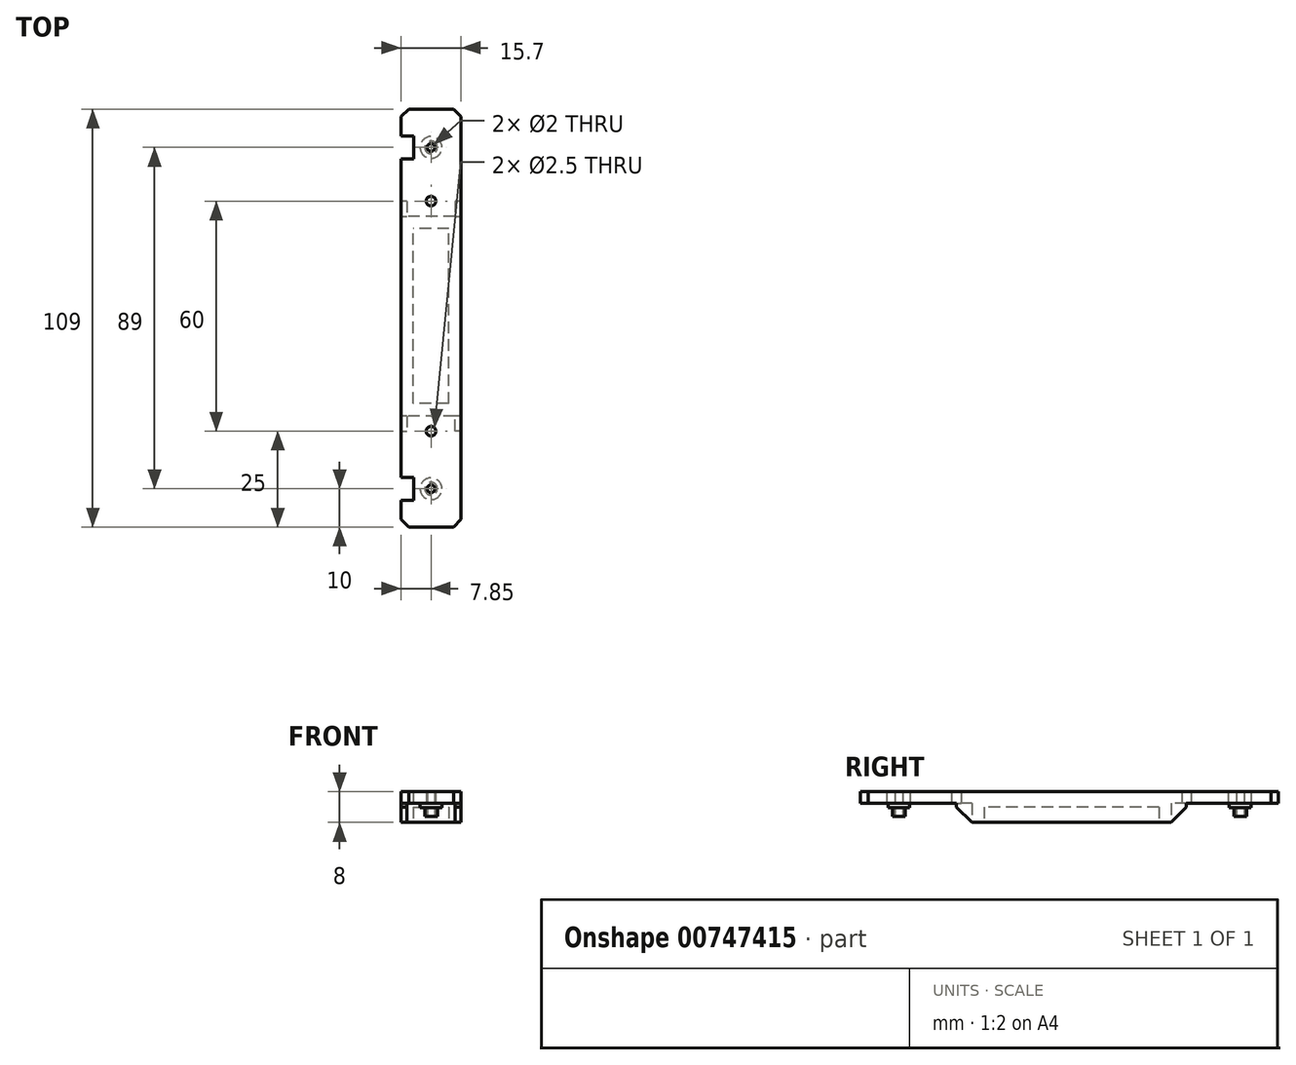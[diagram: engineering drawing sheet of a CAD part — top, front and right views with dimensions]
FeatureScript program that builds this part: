
annotation { "Feature Type Name" : "Feature", "Feature Type Description" : "" }
export const myFeature = defineFeature(function(context is Context, id is Id, definition is map)
    precondition{}
    {
        {
            var Q0;
            Q0=qCreatedBy(makeId("Right.planeOp"),FACE);
            var sketch = newSketch(context, id + "F0", { "sketchPlane" : qUnion([Q0])});
            skLineSegment(sketch, "E0", {"start": v(-25, 5) * mm, "end": v(0, 5) * mm});
            skLineSegment(sketch, "E1", {"start": v(0, 5) * mm, "end": v(0, 0) * mm});
            skLineSegment(sketch, "E2", {"start": v(60, 0) * mm, "end": v(60, 5) * mm});
            skLineSegment(sketch, "E3", {"start": v(60, 5) * mm, "end": v(84, 5) * mm});
            skLineSegment(sketch, "E4", {"start": v(84, 5) * mm, "end": v(84, 8) * mm});
            skLineSegment(sketch, "E5", {"start": v(-25, 8) * mm, "end": v(-25, 5) * mm});
            skLineSegment(sketch, "E6.trimOffspring", {"start": v(84, 8) * mm, "end": v(-25, 8) * mm});
            skLineSegment(sketch, "E7", {"start": v(0, 0) * mm, "end": v(0, 0) * mm});
            skLineSegment(sketch, "E8", {"start": v(0, 0) * mm, "end": v(60, 0) * mm});
            skSolve(sketch);
        }
        {
            var Q0;
            Q0=qSketchRegion(id+"F0",true);
            extrude(context, id + "F1", {"entities" : qUnion([Q0]), "depth" : 15.7 * mm, "offsetDistance" : 25 * mm, "symmetric" : true});
        }
        {
            var Q0;
            Q0=makeQuery(id+"F1.opExtrude","CAP_EDGE",EDGE,{"disambiguationData":[OSD([sQuery(id+"F0.wireOp",EDGE,"E5")])],"isStart":false});
            var Q1;
            Q1=makeQuery(id+"F1.opExtrude","CAP_EDGE",EDGE,{"disambiguationData":[OSD([sQuery(id+"F0.wireOp",EDGE,"E5")])],"isStart":true});
            var Q2;
            Q2=makeQuery(id+"F1.opExtrude","CAP_EDGE",EDGE,{"disambiguationData":[OSD([sQuery(id+"F0.wireOp",EDGE,"E4")])],"isStart":false});
            var Q3;
            Q3=makeQuery(id+"F1.opExtrude","CAP_EDGE",EDGE,{"disambiguationData":[OSD([sQuery(id+"F0.wireOp",EDGE,"E4")])],"isStart":true});
            chamfer(context, id + "F2", {"entities" : qUnion([Q0, Q1, Q2, Q3]), "width" : 2 * mm, "tangentPropagation" : true});
        }
        {
            var Q0;
            Q0=makeQuery(id+"F1.opExtrude","SWEPT_FACE",FACE,{"disambiguationData":[OSD([sQuery(id+"F0.wireOp",EDGE,"E0")])]});
            var sketch = newSketch(context, id + "F3", { "sketchPlane" : qUnion([Q0])});
            skCircle(sketch, "E9", {"center": v(0, 15) * mm, "radius": 1 * mm});
            skCircle(sketch, "E10", {"center": v(0, -74) * mm, "radius": 1 * mm});
            skLineSegment(sketch, "E11", {"start": v(0, 15) * mm, "end": v(0, 0) * mm, "construction": true});
            skLineSegment(sketch, "E12", {"start": v(0, 0) * mm, "end": v(0, -74) * mm, "construction": true});
            skLineSegment(sketch, "E13", {"start": v(0, 15) * mm, "end": v(0, 25) * mm, "construction": true});
            skLineSegment(sketch, "E14", {"start": v(0, -74) * mm, "end": v(0, -84) * mm, "construction": true});
            skSolve(sketch);
        }
        {
            var Q0;
            Q0=qSketchRegion(id+"F3",true);
            extrude(context, id + "F4", {"entities" : qUnion([Q0]), "operationType" : NewBodyOperationType.REMOVE, "endBound" : BoundingType.UP_TO_NEXT, "oppositeDirection" : true, "depth" : 25 * mm, "offsetDistance" : 25 * mm});
        }
        {
            var Q0;
            Q0=makeQuery(id+"F1.opExtrude","SWEPT_FACE",FACE,{"disambiguationData":[OSD([sQuery(id+"F0.wireOp",EDGE,"E7"),sQuery(id+"F0.wireOp",EDGE,"E8")])]});
            var sketch = newSketch(context, id + "F5", { "sketchPlane" : qUnion([Q0])});
            skLineSegment(sketch, "E15", {"start": v(6.25, 0) * mm, "end": v(-6.25, 0) * mm});
            skPoint(sketch, "E16.orphan", {"position": v(0, -4) * mm});
            skLineSegment(sketch, "E17", {"start": v(0, 0) * mm, "end": v(0, -4) * mm, "construction": true});
            skLineSegment(sketch, "E18", {"start": v(6.25, 0) * mm, "end": v(6.25, -4) * mm});
            skLineSegment(sketch, "E19", {"start": v(6.25, -4) * mm, "end": v(-6.25, -4) * mm});
            skLineSegment(sketch, "E20", {"start": v(-6.25, -4) * mm, "end": v(-6.25, 0) * mm});
            skLineSegment(sketch, "E21.bottom", {"start": v(6.25, -60) * mm, "end": v(-6.25, -60) * mm});
            skLineSegment(sketch, "E21.top", {"start": v(6.25, -56) * mm, "end": v(-6.25, -56) * mm});
            skLineSegment(sketch, "E21.left", {"start": v(6.25, -60) * mm, "end": v(6.25, -56) * mm});
            skLineSegment(sketch, "E21.right", {"start": v(-6.25, -60) * mm, "end": v(-6.25, -56) * mm});
            skSolve(sketch);
        }
        {
            var Q0;
            Q0=qSketchRegion(id+"F5",true);
            var Q1;
            Q1=makeQuery(id+"F1.opExtrude","SWEPT_FACE",FACE,{"disambiguationData":[OSD([sQuery(id+"F0.wireOp",EDGE,"E0")])]});
            extrude(context, id + "F6", {"entities" : qUnion([Q0]), "operationType" : NewBodyOperationType.REMOVE, "endBound" : BoundingType.UP_TO_SURFACE, "oppositeDirection" : true, "depth" : 25 * mm, "endBoundEntityFace" : qUnion([Q1]), "offsetDistance" : 25 * mm});
        }
        {
            var Q0;
            {Q0=qUnion([makeQuery(id+"F6.boolean.opBoolean","MERGE",FACE,{"derivedFrom":[makeQuery(id+"F1.opExtrude","SWEPT_FACE",FACE,{"disambiguationData":[OSD([sQuery(id+"F0.wireOp",EDGE,"E0")])]})],"fromTools":[makeQuery(id+"F6.opExtrude","CAP_FACE",FACE,{"disambiguationData":[OSD([sQuery(id+"F5.wireOp",EDGE,"QtaLUQ9K-xFjA-aVn2-jr8E-2nqdviAdBmNi"),sQuery(id+"F5.wireOp",EDGE,"MIOGkYBv-3kq0-NffD-4QcD-ZkNMdwIdXdjM"),sQuery(id+"F5.wireOp",EDGE,"E15"),sQuery(id+"F5.wireOp",EDGE,"Q6Nk2F50-RIht-aVqs-q8m5-kIFtcKPUQnbz")])],"isStart":false})]}),makeQuery(id+"F6.boolean.opBoolean","MERGE",FACE,{"derivedFrom":[makeQuery(id+"F1.opExtrude","SWEPT_FACE",FACE,{"disambiguationData":[OSD([sQuery(id+"F0.wireOp",EDGE,"E3")])]})],"fromTools":[makeQuery(id+"F6.opExtrude","CAP_FACE",FACE,{"disambiguationData":[OSD([sQuery(id+"F5.wireOp",EDGE,"UIq0axqO-XxSW-t0FF-EL4X-YCJ9C5suXqDZ"),sQuery(id+"F5.wireOp",EDGE,"48w0VJL2-kqmk-4goN-fqhj-BqvBEsziLtPm"),sQuery(id+"F5.wireOp",EDGE,"iuIQCKwA-ER4D-4RKV-h3Pt-EvZXLoRTW6qv"),sQuery(id+"F5.wireOp",EDGE,"zWaE9cvL-vTQC-7oDd-e5Ol-owMjjvXLEkyw")])],"isStart":false})]})]);}
            var sketch = newSketch(context, id + "F7", { "sketchPlane" : qUnion([Q0])});
            skCircle(sketch, "E22", {"center": v(0, 0) * mm, "radius": 1.25 * mm});
            skCircle(sketch, "E23", {"center": v(0, -60) * mm, "radius": 1.25 * mm});
            skLineSegment(sketch, "E24", {"start": v(0, 0) * mm, "end": v(0, -4) * mm, "construction": true});
            skLineSegment(sketch, "E25", {"start": v(0, -60) * mm, "end": v(0, -56) * mm, "construction": true});
            skSolve(sketch);
        }
        {
            var Q0;
            Q0=qSketchRegion(id+"F7",true);
            extrude(context, id + "F8", {"entities" : qUnion([Q0]), "operationType" : NewBodyOperationType.REMOVE, "endBound" : BoundingType.UP_TO_NEXT, "oppositeDirection" : true, "depth" : 25 * mm, "offsetDistance" : 25 * mm});
        }
        {
            var Q0;
            Q0=makeQuery(id+"F6.boolean.opBoolean","MERGE",FACE,{"derivedFrom":[makeQuery(id+"F1.opExtrude","SWEPT_FACE",FACE,{"disambiguationData":[OSD([sQuery(id+"F0.wireOp",EDGE,"E3")])]})],"fromTools":[makeQuery(id+"F6.opExtrude","CAP_FACE",FACE,{"disambiguationData":[OSD([sQuery(id+"F5.wireOp",EDGE,"UIq0axqO-XxSW-t0FF-EL4X-YCJ9C5suXqDZ"),sQuery(id+"F5.wireOp",EDGE,"48w0VJL2-kqmk-4goN-fqhj-BqvBEsziLtPm"),sQuery(id+"F5.wireOp",EDGE,"iuIQCKwA-ER4D-4RKV-h3Pt-EvZXLoRTW6qv")])],"isStart":false})]});
            var sketch = newSketch(context, id + "F9", { "sketchPlane" : qUnion([Q0])});
            skCircle(sketch, "E26", {"center": v(0, -74) * mm, "radius": 1.65 * mm});
            skCircle(sketch, "E27", {"center": v(0, 15) * mm, "radius": 1.65 * mm});
            skCircle(sketch, "E28.0", {"center": v(0, -74) * mm, "radius": 1 * mm});
            skCircle(sketch, "E29.0", {"center": v(0, 15) * mm, "radius": 1 * mm});
            skSolve(sketch);
        }
        {
            var Q0;
            Q0=qSketchRegion(id+"F9",true);
            extrude(context, id + "F10", {"entities" : qUnion([Q0]), "operationType" : NewBodyOperationType.ADD, "depth" : 3.5 * mm, "offsetDistance" : 25 * mm});
        }
        {
            var Q0;
            Q0=makeQuery(id+"F1.opExtrude","SWEPT_FACE",FACE,{"disambiguationData":[OSD([sQuery(id+"F0.wireOp",EDGE,"E6.trimOffspring")])]});
            var sketch = newSketch(context, id + "F11", { "sketchPlane" : qUnion([Q0])});
            skLineSegment(sketch, "E30", {"start": v(-7.85, -12) * mm, "end": v(-4.5, -12) * mm});
            skLineSegment(sketch, "E31", {"start": v(-4.5, -12) * mm, "end": v(-4.5, -18) * mm});
            skLineSegment(sketch, "E32", {"start": v(-4.5, -18) * mm, "end": v(-7.85, -18) * mm});
            skLineSegment(sketch, "E33", {"start": v(-7.85, -18) * mm, "end": v(-7.85, -12) * mm});
            skLineSegment(sketch, "E34", {"start": v(0, -15) * mm, "end": v(0, -7.98) * mm, "construction": true});
            skLineSegment(sketch, "E35", {"start": v(0, -15) * mm, "end": v(-4.5, -15) * mm, "construction": true});
            skLineSegment(sketch, "E36.bottom", {"start": v(-7.85, 71) * mm, "end": v(-4.5, 71) * mm});
            skLineSegment(sketch, "E36.top", {"start": v(-7.85, 77) * mm, "end": v(-4.5, 77) * mm});
            skLineSegment(sketch, "E36.left", {"start": v(-7.85, 71) * mm, "end": v(-7.85, 77) * mm});
            skLineSegment(sketch, "E36.right", {"start": v(-4.5, 71) * mm, "end": v(-4.5, 77) * mm});
            skLineSegment(sketch, "E37", {"start": v(-4.5, 74) * mm, "end": v(0, 74) * mm, "construction": true});
            skSolve(sketch);
        }
        {
            var Q0;
            Q0=qSketchRegion(id+"F11",true);
            extrude(context, id + "F12", {"entities" : qUnion([Q0]), "operationType" : NewBodyOperationType.REMOVE, "endBound" : BoundingType.UP_TO_NEXT, "oppositeDirection" : true, "depth" : 25 * mm, "offsetDistance" : 25 * mm});
        }
        {
            var Q0;
            Q0=makeQuery(id+"F6.boolean.opBoolean","MERGE",FACE,{"derivedFrom":[makeQuery(id+"F1.opExtrude","SWEPT_FACE",FACE,{"disambiguationData":[OSD([sQuery(id+"F0.wireOp",EDGE,"E3")])]})],"fromTools":[makeQuery(id+"F6.opExtrude","CAP_FACE",FACE,{"disambiguationData":[OSD([sQuery(id+"F5.wireOp",EDGE,"UIq0axqO-XxSW-t0FF-EL4X-YCJ9C5suXqDZ"),sQuery(id+"F5.wireOp",EDGE,"48w0VJL2-kqmk-4goN-fqhj-BqvBEsziLtPm"),sQuery(id+"F5.wireOp",EDGE,"iuIQCKwA-ER4D-4RKV-h3Pt-EvZXLoRTW6qv")])],"isStart":false})]});
            var sketch = newSketch(context, id + "F13", { "sketchPlane" : qUnion([Q0])});
            skCircle(sketch, "E38", {"center": v(0, -74) * mm, "radius": 2.85 * mm});
            skCircle(sketch, "E39", {"center": v(0, 15) * mm, "radius": 2.85 * mm});
            skCircle(sketch, "E40.0", {"center": v(0, 15) * mm, "radius": 1 * mm});
            skCircle(sketch, "E40.1", {"center": v(0, -74) * mm, "radius": 1 * mm});
            skSolve(sketch);
        }
        {
            var Q0;
            Q0=qSketchRegion(id+"F13",true);
            extrude(context, id + "F14", {"entities" : qUnion([Q0]), "operationType" : NewBodyOperationType.ADD, "depth" : 1.2 * mm, "offsetDistance" : 25 * mm});
        }
        {
            var Q0;
            Q0=makeQuery(id+"F1.opExtrude","SWEPT_FACE",FACE,{"disambiguationData":[OSD([sQuery(id+"F0.wireOp",EDGE,"E8")])]});
            var sketch = newSketch(context, id + "F15", { "sketchPlane" : qUnion([Q0])});
            skLineSegment(sketch, "E41.bottom", {"start": v(4.65, -7.2) * mm, "end": v(-4.65, -7.2) * mm});
            skLineSegment(sketch, "E41.top", {"start": v(4.65, -52.8) * mm, "end": v(-4.65, -52.8) * mm});
            skLineSegment(sketch, "E41.left", {"start": v(4.65, -7.2) * mm, "end": v(4.65, -52.8) * mm});
            skLineSegment(sketch, "E41.right", {"start": v(-4.65, -7.2) * mm, "end": v(-4.65, -52.8) * mm});
            skLineSegment(sketch, "E42", {"start": v(4.65, -30) * mm, "end": v(7.85, -30) * mm, "construction": true});
            skLineSegment(sketch, "E43", {"start": v(-4.65, -30) * mm, "end": v(-7.85, -30) * mm, "construction": true});
            skSolve(sketch);
        }
        {
            var Q0;
            Q0=qSketchRegion(id+"F15",true);
            var Q1;
            Q1=makeQuery(id+"F1.opExtrude","SWEPT_FACE",FACE,{"disambiguationData":[OSD([sQuery(id+"F0.wireOp",EDGE,"E6.trimOffspring")])]});
            extrude(context, id + "F16", {"entities" : qUnion([Q0]), "operationType" : NewBodyOperationType.REMOVE, "endBound" : BoundingType.UP_TO_SURFACE, "oppositeDirection" : true, "depth" : 25 * mm, "endBoundEntityFace" : qUnion([Q1]), "hasOffset" : true, "offsetDistance" : 4 * mm});
        }
        {
            var Q0;
            {var subQ0=sQuery(id+"F0.wireOp",EDGE,"E8");var subQ1=sQuery(id+"F0.wireOp",EDGE,"E1");Q0=makeQuery(id+"F6.boolean.opBoolean","SPLIT",EDGE,{"disambiguationData":[TD([makeQuery(id+"F6.opExtrude","SWEPT_FACE",FACE,{"disambiguationData":[OSD([sQuery(id+"F5.wireOp",EDGE,"E20")])]})])],"derivedFrom":makeQuery(id+"F1.opExtrude","SWEPT_EDGE",EDGE,{"disambiguationData":[OSD([subQ1,subQ0])]})});}
            var Q1;
            {var subQ0=sQuery(id+"F0.wireOp",EDGE,"E8");var subQ1=sQuery(id+"F0.wireOp",EDGE,"E1");Q1=makeQuery(id+"F6.boolean.opBoolean","SPLIT",EDGE,{"disambiguationData":[TD([makeQuery(id+"F6.opExtrude","SWEPT_FACE",FACE,{"disambiguationData":[OSD([sQuery(id+"F5.wireOp",EDGE,"E18")])]})])],"derivedFrom":makeQuery(id+"F1.opExtrude","SWEPT_EDGE",EDGE,{"disambiguationData":[OSD([subQ1,subQ0])]})});}
            var Q2;
            {var subQ0=sQuery(id+"F0.wireOp",EDGE,"E8");var subQ1=sQuery(id+"F0.wireOp",EDGE,"E2");Q2=makeQuery(id+"F6.boolean.opBoolean","SPLIT",EDGE,{"disambiguationData":[TD([makeQuery(id+"F6.opExtrude","SWEPT_FACE",FACE,{"disambiguationData":[OSD([sQuery(id+"F5.wireOp",EDGE,"E21.right")])]})])],"derivedFrom":makeQuery(id+"F1.opExtrude","SWEPT_EDGE",EDGE,{"disambiguationData":[OSD([subQ1,subQ0])]})});}
            var Q3;
            {var subQ0=sQuery(id+"F0.wireOp",EDGE,"E8");var subQ1=sQuery(id+"F0.wireOp",EDGE,"E2");Q3=makeQuery(id+"F6.boolean.opBoolean","SPLIT",EDGE,{"disambiguationData":[TD([makeQuery(id+"F6.opExtrude","SWEPT_FACE",FACE,{"disambiguationData":[OSD([sQuery(id+"F5.wireOp",EDGE,"E21.left")])]})])],"derivedFrom":makeQuery(id+"F1.opExtrude","SWEPT_EDGE",EDGE,{"disambiguationData":[OSD([subQ1,subQ0])]})});}
            chamfer(context, id + "F17", {"entities" : qUnion([Q0, Q1, Q2, Q3]), "width" : 4 * mm, "tangentPropagation" : true});
        }
    });
